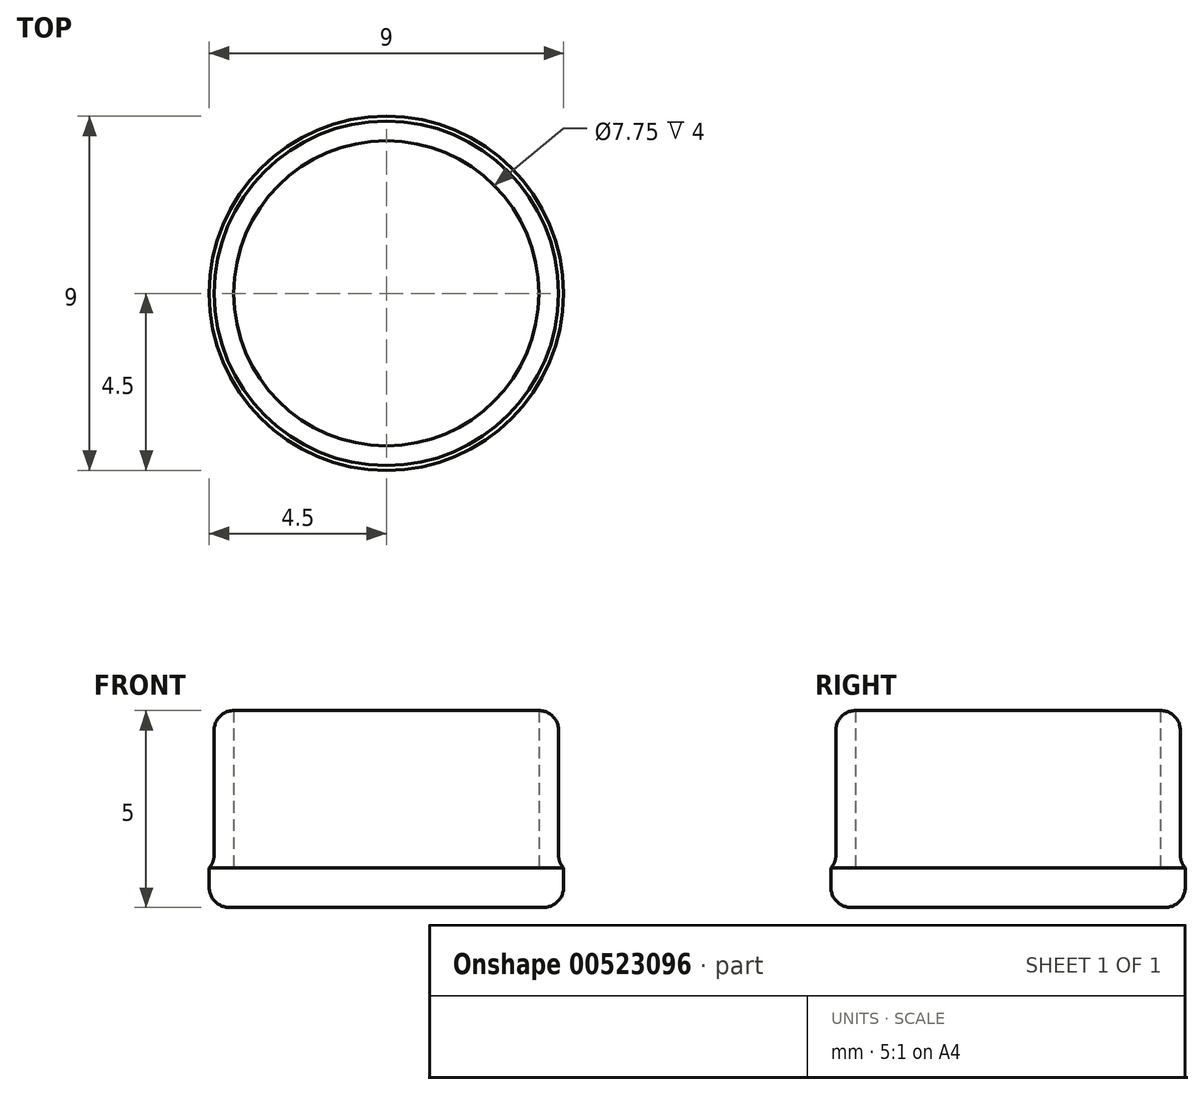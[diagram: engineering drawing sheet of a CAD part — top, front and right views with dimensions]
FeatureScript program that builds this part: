
annotation { "Feature Type Name" : "Feature", "Feature Type Description" : "" }
export const myFeature = defineFeature(function(context is Context, id is Id, definition is map)
    precondition{}
    {
        {
            var Q0;
            Q0=qCreatedBy(makeId("Top.planeOp"),FACE);
            var sketch = newSketch(context, id + "F0", { "sketchPlane" : qUnion([Q0])});
            skCircle(sketch, "E0", {"center": v(0, 0) * mm, "radius": 5 * mm});
            skCircle(sketch, "E1", {"center": v(0, 0) * mm, "radius": 4.38 * mm});
            skCircle(sketch, "E2", {"center": v(0, 0) * mm, "radius": 3.88 * mm});
            skSolve(sketch);
        }
        {
            var Q0;
            Q0=makeQuery(id+"F0.imprint","IMPRINT",FACE,{"disambiguationData":[TD([[makeQuery(id+"F0.imprint","IMPRINT",EDGE,{"derivedFrom":sQuery(id+"F0.wireOp",EDGE,"E1")}),1.0]])]});
            extrude(context, id + "F1", {"entities" : qUnion([Q0]), "depth" : 4 * mm, "offsetDistance" : 25 * mm});
        }
        {
            var Q0;
            Q0=qCreatedBy(makeId("Top.planeOp"),FACE);
            var sketch = newSketch(context, id + "F2", { "sketchPlane" : qUnion([Q0])});
            skCircle(sketch, "E3", {"center": v(0, 0) * mm, "radius": 4.5 * mm});
            skSolve(sketch);
        }
        {
            var Q0;
            Q0 = qSketchRegion(id + "F2", true);
            extrude(context, id + "F3", {"entities" : qUnion([Q0]), "operationType" : NewBodyOperationType.ADD, "depth" : 0 * mm, "offsetDistance" : 25 * mm, "hasSecondDirection" : true, "secondDirectionOppositeDirection" : true, "secondDirectionDepth" : 1 * mm});
        }
        {
            var Q0;
            Q0=makeQuery(id+"F3.opExtrude","CAP_EDGE",EDGE,{"disambiguationData":[OSD([sQuery(id+"F2.wireOp",EDGE,"E3")])],"isStart":true});
            var Q1;
            Q1=makeQuery(id+"F1.opExtrude","CAP_EDGE",EDGE,{"disambiguationData":[OSD([sQuery(id+"F0.wireOp",EDGE,"E1")])],"isStart":true});
            fillet(context, id + "F4", {"entities" : qUnion([Q0, Q1]), "radius" : 0.5 * mm, "tangentPropagation" : true, "allowEdgeOverflow" : false});
        }
        {
            var Q0;
            Q0=makeQuery(id+"F1.opExtrude","SWEPT_FACE",FACE,{"disambiguationData":[OSD([sQuery(id+"F0.wireOp",EDGE,"E1")])]});
            fillet(context, id + "F5", {"entities" : qUnion([Q0]), "radius" : 0.5 * mm, "tangentPropagation" : true, "allowEdgeOverflow" : false});
        }
    });
